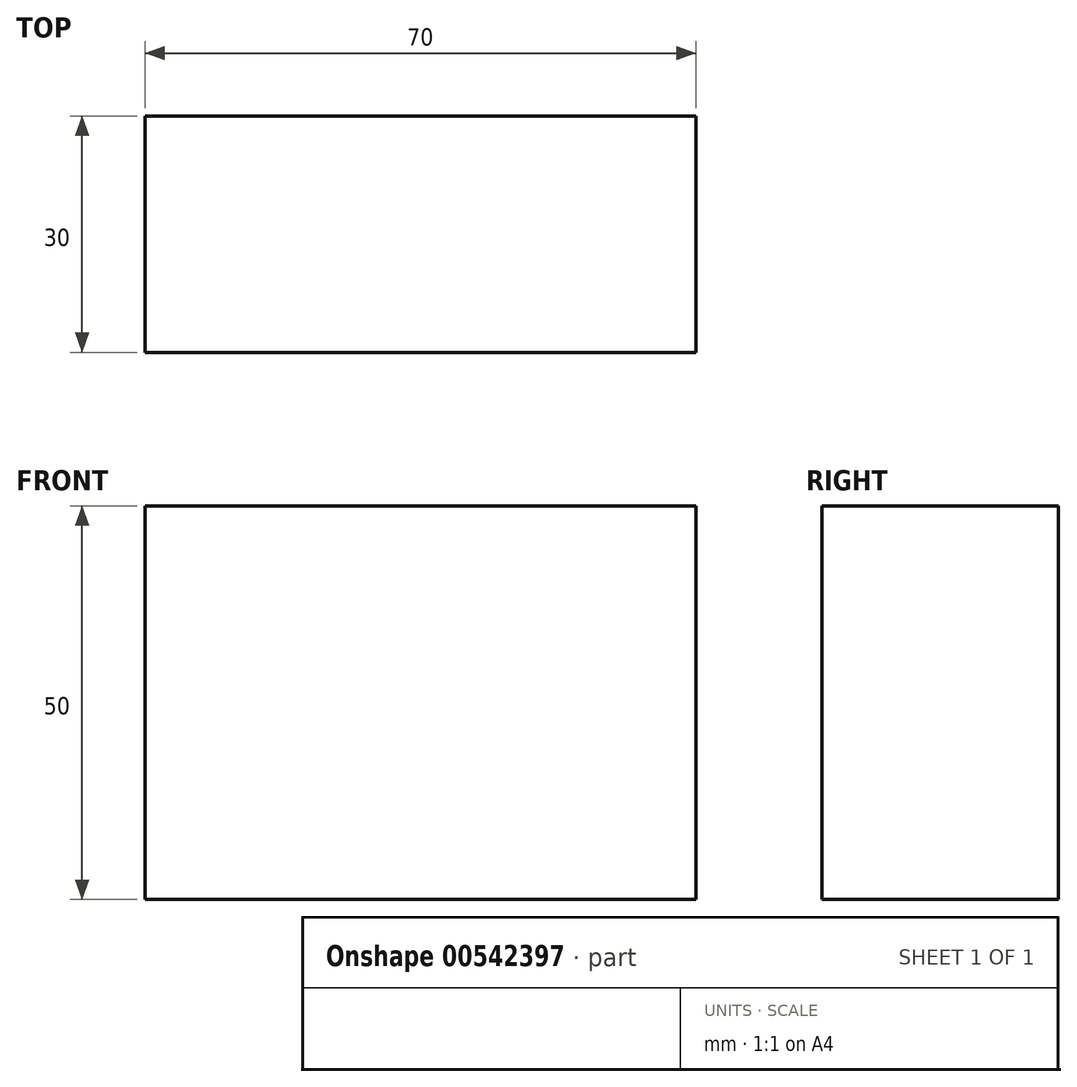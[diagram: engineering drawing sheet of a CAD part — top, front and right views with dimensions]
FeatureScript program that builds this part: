
annotation { "Feature Type Name" : "Feature", "Feature Type Description" : "" }
export const myFeature = defineFeature(function(context is Context, id is Id, definition is map)
    precondition{}
    {
        {
            var Q0;
            Q0=qCreatedBy(makeId("Front.planeOp"),FACE);
            var sketch = newSketch(context, id + "F0", { "sketchPlane" : qUnion([Q0])});
            skLineSegment(sketch, "E0", {"start": v(-32.95, 20.27) * mm, "end": v(37.05, 20.27) * mm});
            skLineSegment(sketch, "E1", {"start": v(37.05, 20.27) * mm, "end": v(37.05, -29.73) * mm});
            skLineSegment(sketch, "E2", {"start": v(37.05, -29.73) * mm, "end": v(-32.95, -29.73) * mm});
            skLineSegment(sketch, "E3", {"start": v(-32.95, -29.73) * mm, "end": v(-32.95, 20.27) * mm});
            skSolve(sketch);
        }
        {
            var Q0;
            Q0=makeQuery(id+"F0.imprint","IMPRINT",FACE,{"disambiguationData":[TD([[makeQuery(id+"F0.imprint","IMPRINT",EDGE,{"derivedFrom":sQuery(id+"F0.wireOp",EDGE,"E0")}),-1.0]])]});
            extrude(context, id + "F1", {"entities" : qUnion([Q0]), "depth" : 30 * mm, "offsetDistance" : 25 * mm});
        }
    });
